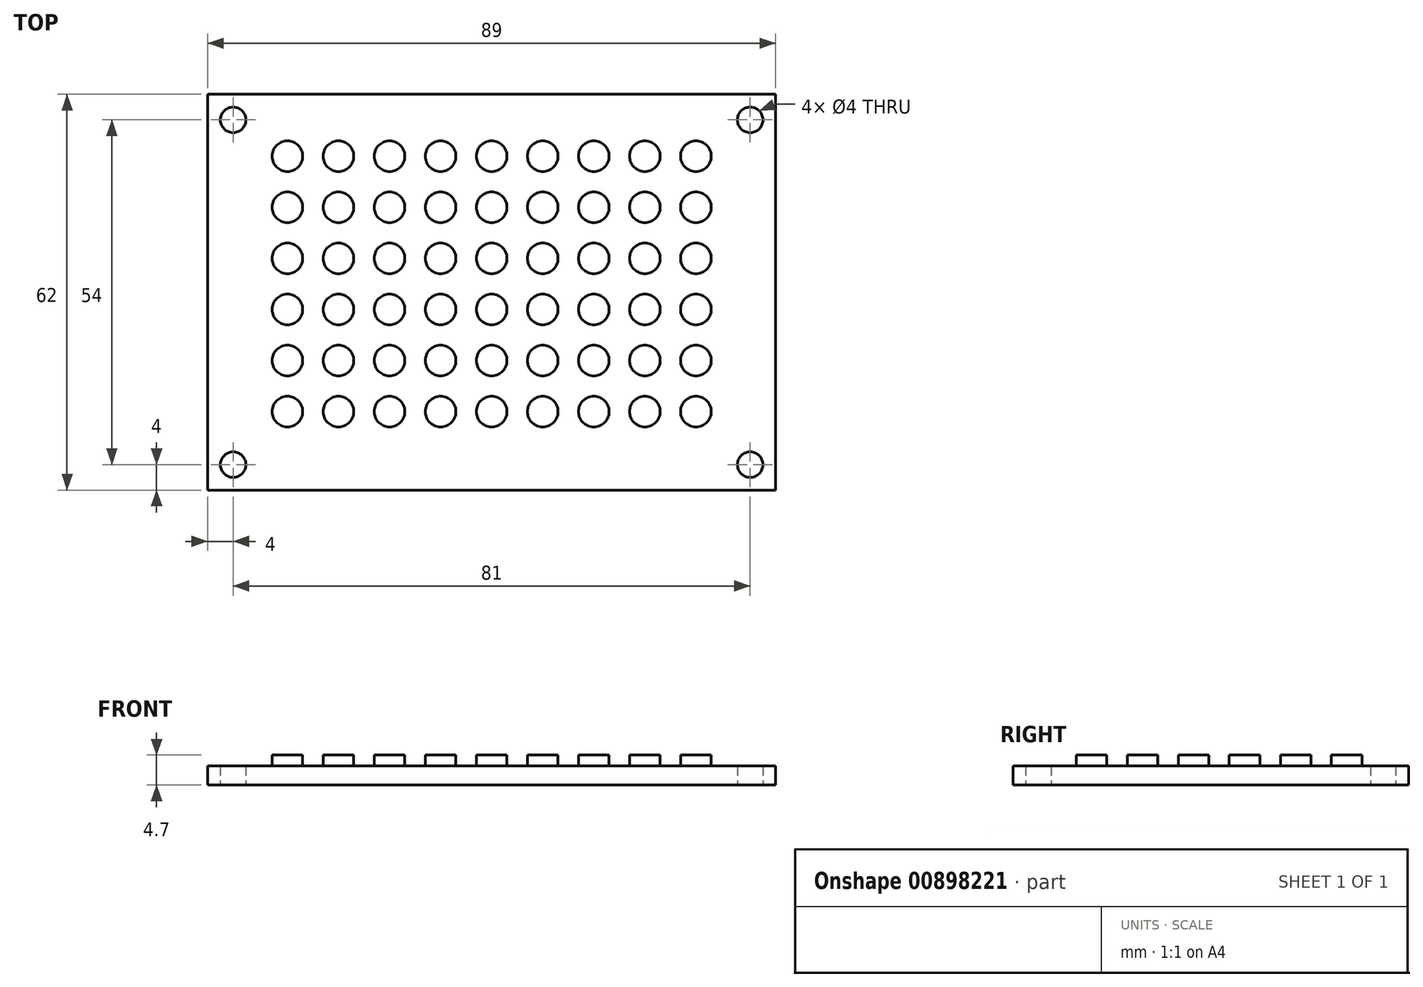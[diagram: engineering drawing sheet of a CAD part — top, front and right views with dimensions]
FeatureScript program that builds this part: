
annotation { "Feature Type Name" : "Feature", "Feature Type Description" : "" }
export const myFeature = defineFeature(function(context is Context, id is Id, definition is map)
    precondition{}
    {
        {
            var Q0;
            Q0=qCreatedBy(makeId("Top.planeOp"),FACE);
            var sketch = newSketch(context, id + "F0", { "sketchPlane" : qUnion([Q0])});
            skLineSegment(sketch, "E0.bottom", {"start": v(44.5, -31) * mm, "end": v(-44.5, -31) * mm});
            skLineSegment(sketch, "E0.top", {"start": v(44.5, 31) * mm, "end": v(-44.5, 31) * mm});
            skLineSegment(sketch, "E0.left", {"start": v(44.5, -31) * mm, "end": v(44.5, 31) * mm});
            skLineSegment(sketch, "E0.right", {"start": v(-44.5, -31) * mm, "end": v(-44.5, 31) * mm});
            skPoint(sketch, "E0.middle", {"position": v(0, 0) * mm});
            skCircle(sketch, "E1", {"center": v(40.5, 27) * mm, "radius": 2 * mm});
            skCircle(sketch, "E2.MirrorC", {"center": v(-40.5, 27) * mm, "radius": 2 * mm});
            skPoint(sketch, "E3.endSnap0", {"position": v(44.5, 0) * mm});
            skCircle(sketch, "E4.MirrorC", {"center": v(40.5, -27) * mm, "radius": 2 * mm});
            skCircle(sketch, "E5.MirrorC", {"center": v(-40.5, -27) * mm, "radius": 2 * mm});
            skSolve(sketch);
        }
        {
            var Q0;
            Q0=makeQuery(id+"F0.imprint","IMPRINT",FACE,{"disambiguationData":[TD([[makeQuery(id+"F0.imprint","IMPRINT",EDGE,{"derivedFrom":sQuery(id+"F0.wireOp",EDGE,"E0.bottom")}),-1.0]])]});
            extrude(context, id + "F1", {"entities" : qUnion([Q0]), "depth" : 3 * mm, "offsetDistance" : 25 * mm});
        }
        {
            var Q0;
            Q0=makeQuery(id+"F1.opExtrude","CAP_FACE",FACE,{"disambiguationData":[OSD([sQuery(id+"F0.wireOp",EDGE,"E0.bottom"),sQuery(id+"F0.wireOp",EDGE,"E0.top"),sQuery(id+"F0.wireOp",EDGE,"E0.left"),sQuery(id+"F0.wireOp",EDGE,"E0.right"),sQuery(id+"F0.wireOp",EDGE,"E2.MirrorC"),sQuery(id+"F0.wireOp",EDGE,"E4.MirrorC"),sQuery(id+"F0.wireOp",EDGE,"E1"),sQuery(id+"F0.wireOp",EDGE,"E5.MirrorC")])],"isStart":false});
            var sketch = newSketch(context, id + "F2", { "sketchPlane" : qUnion([Q0])});
            skCircle(sketch, "E6", {"center": v(0, 21.3) * mm, "radius": 2.4 * mm});
            skCircle(sketch, "E7.1.0.0", {"center": v(8, 21.3) * mm, "radius": 2.4 * mm});
            skCircle(sketch, "E7.2.0.0", {"center": v(16, 21.3) * mm, "radius": 2.4 * mm});
            skCircle(sketch, "E7.3.0.0", {"center": v(24, 21.3) * mm, "radius": 2.4 * mm});
            skCircle(sketch, "E7.4.0.0", {"center": v(32, 21.3) * mm, "radius": 2.4 * mm});
            skCircle(sketch, "E8.1.0.0", {"center": v(-8, 21.3) * mm, "radius": 2.4 * mm});
            skCircle(sketch, "E8.2.0.0", {"center": v(-16, 21.3) * mm, "radius": 2.4 * mm});
            skCircle(sketch, "E8.3.0.0", {"center": v(-24, 21.3) * mm, "radius": 2.4 * mm});
            skCircle(sketch, "E8.4.0.0", {"center": v(-32, 21.3) * mm, "radius": 2.4 * mm});
            skCircle(sketch, "E9.1.0.0", {"center": v(-8, 13.3) * mm, "radius": 2.4 * mm});
            skCircle(sketch, "E9.1.0.1", {"center": v(32, 13.3) * mm, "radius": 2.4 * mm});
            skCircle(sketch, "E9.1.0.2", {"center": v(8, 13.3) * mm, "radius": 2.4 * mm});
            skCircle(sketch, "E9.1.0.3", {"center": v(-32, 13.3) * mm, "radius": 2.4 * mm});
            skCircle(sketch, "E9.1.0.4", {"center": v(24, 13.3) * mm, "radius": 2.4 * mm});
            skCircle(sketch, "E9.1.0.5", {"center": v(16, 13.3) * mm, "radius": 2.4 * mm});
            skCircle(sketch, "E9.1.0.6", {"center": v(-24, 13.3) * mm, "radius": 2.4 * mm});
            skCircle(sketch, "E9.1.0.7", {"center": v(-16, 13.3) * mm, "radius": 2.4 * mm});
            skCircle(sketch, "E9.1.0.8", {"center": v(0, 13.3) * mm, "radius": 2.4 * mm});
            skCircle(sketch, "E9.2.0.0", {"center": v(-8, 5.3) * mm, "radius": 2.4 * mm});
            skCircle(sketch, "E9.2.0.1", {"center": v(32, 5.3) * mm, "radius": 2.4 * mm});
            skCircle(sketch, "E9.2.0.2", {"center": v(8, 5.3) * mm, "radius": 2.4 * mm});
            skCircle(sketch, "E9.2.0.3", {"center": v(-32, 5.3) * mm, "radius": 2.4 * mm});
            skCircle(sketch, "E9.2.0.4", {"center": v(24, 5.3) * mm, "radius": 2.4 * mm});
            skCircle(sketch, "E9.2.0.5", {"center": v(16, 5.3) * mm, "radius": 2.4 * mm});
            skCircle(sketch, "E9.2.0.6", {"center": v(-24, 5.3) * mm, "radius": 2.4 * mm});
            skCircle(sketch, "E9.2.0.7", {"center": v(-16, 5.3) * mm, "radius": 2.4 * mm});
            skCircle(sketch, "E9.2.0.8", {"center": v(0, 5.3) * mm, "radius": 2.4 * mm});
            skCircle(sketch, "E9.3.0.0", {"center": v(-8, -2.7) * mm, "radius": 2.4 * mm});
            skCircle(sketch, "E9.3.0.1", {"center": v(32, -2.7) * mm, "radius": 2.4 * mm});
            skCircle(sketch, "E9.3.0.2", {"center": v(8, -2.7) * mm, "radius": 2.4 * mm});
            skCircle(sketch, "E9.3.0.3", {"center": v(-32, -2.7) * mm, "radius": 2.4 * mm});
            skCircle(sketch, "E9.3.0.4", {"center": v(24, -2.7) * mm, "radius": 2.4 * mm});
            skCircle(sketch, "E9.3.0.5", {"center": v(16, -2.7) * mm, "radius": 2.4 * mm});
            skCircle(sketch, "E9.3.0.6", {"center": v(-24, -2.7) * mm, "radius": 2.4 * mm});
            skCircle(sketch, "E9.3.0.7", {"center": v(-16, -2.7) * mm, "radius": 2.4 * mm});
            skCircle(sketch, "E9.3.0.8", {"center": v(0, -2.7) * mm, "radius": 2.4 * mm});
            skCircle(sketch, "E9.4.0.0", {"center": v(-8, -10.7) * mm, "radius": 2.4 * mm});
            skCircle(sketch, "E9.4.0.1", {"center": v(32, -10.7) * mm, "radius": 2.4 * mm});
            skCircle(sketch, "E9.4.0.2", {"center": v(8, -10.7) * mm, "radius": 2.4 * mm});
            skCircle(sketch, "E9.4.0.3", {"center": v(-32, -10.7) * mm, "radius": 2.4 * mm});
            skCircle(sketch, "E9.4.0.4", {"center": v(24, -10.7) * mm, "radius": 2.4 * mm});
            skCircle(sketch, "E9.4.0.5", {"center": v(16, -10.7) * mm, "radius": 2.4 * mm});
            skCircle(sketch, "E9.4.0.6", {"center": v(-24, -10.7) * mm, "radius": 2.4 * mm});
            skCircle(sketch, "E9.4.0.7", {"center": v(-16, -10.7) * mm, "radius": 2.4 * mm});
            skCircle(sketch, "E9.4.0.8", {"center": v(0, -10.7) * mm, "radius": 2.4 * mm});
            skCircle(sketch, "E9.5.0.0", {"center": v(-8, -18.7) * mm, "radius": 2.4 * mm});
            skCircle(sketch, "E9.5.0.1", {"center": v(32, -18.7) * mm, "radius": 2.4 * mm});
            skCircle(sketch, "E9.5.0.2", {"center": v(8, -18.7) * mm, "radius": 2.4 * mm});
            skCircle(sketch, "E9.5.0.3", {"center": v(-32, -18.7) * mm, "radius": 2.4 * mm});
            skCircle(sketch, "E9.5.0.4", {"center": v(24, -18.7) * mm, "radius": 2.4 * mm});
            skCircle(sketch, "E9.5.0.5", {"center": v(16, -18.7) * mm, "radius": 2.4 * mm});
            skCircle(sketch, "E9.5.0.6", {"center": v(-24, -18.7) * mm, "radius": 2.4 * mm});
            skCircle(sketch, "E9.5.0.7", {"center": v(-16, -18.7) * mm, "radius": 2.4 * mm});
            skCircle(sketch, "E9.5.0.8", {"center": v(0, -18.7) * mm, "radius": 2.4 * mm});
            skLineSegment(sketch, "E9.direction1", {"start": v(-32, 21.3) * mm, "end": v(-32, 13.3) * mm, "construction": true});
            skSolve(sketch);
        }
        {
            var Q0;
            Q0=makeQuery(id+"F2.imprint","IMPRINT",FACE,{"disambiguationData":[TD([[makeQuery(id+"F2.imprint","IMPRINT",EDGE,{"derivedFrom":sQuery(id+"F2.wireOp",EDGE,"E7.2.0.0")}),1.0]])]});
            var Q1;
            Q1=makeQuery(id+"F2.imprint","IMPRINT",FACE,{"disambiguationData":[TD([[makeQuery(id+"F2.imprint","IMPRINT",EDGE,{"derivedFrom":sQuery(id+"F2.wireOp",EDGE,"E7.3.0.0")}),1.0]])]});
            var Q2;
            Q2=makeQuery(id+"F2.imprint","IMPRINT",FACE,{"disambiguationData":[TD([[makeQuery(id+"F2.imprint","IMPRINT",EDGE,{"derivedFrom":sQuery(id+"F2.wireOp",EDGE,"E9.4.0.8")}),1.0]])]});
            var Q3;
            Q3=makeQuery(id+"F2.imprint","IMPRINT",FACE,{"disambiguationData":[TD([[makeQuery(id+"F2.imprint","IMPRINT",EDGE,{"derivedFrom":sQuery(id+"F2.wireOp",EDGE,"E9.5.0.2")}),1.0]])]});
            var Q4;
            Q4=makeQuery(id+"F2.imprint","IMPRINT",FACE,{"disambiguationData":[TD([[makeQuery(id+"F2.imprint","IMPRINT",EDGE,{"derivedFrom":sQuery(id+"F2.wireOp",EDGE,"E9.5.0.4")}),1.0]])]});
            var Q5;
            Q5=makeQuery(id+"F2.imprint","IMPRINT",FACE,{"disambiguationData":[TD([[makeQuery(id+"F2.imprint","IMPRINT",EDGE,{"derivedFrom":sQuery(id+"F2.wireOp",EDGE,"E9.3.0.8")}),1.0]])]});
            var Q6;
            Q6=makeQuery(id+"F2.imprint","IMPRINT",FACE,{"disambiguationData":[TD([[makeQuery(id+"F2.imprint","IMPRINT",EDGE,{"derivedFrom":sQuery(id+"F2.wireOp",EDGE,"E9.4.0.0")}),1.0]])]});
            var Q7;
            Q7=makeQuery(id+"F2.imprint","IMPRINT",FACE,{"disambiguationData":[TD([[makeQuery(id+"F2.imprint","IMPRINT",EDGE,{"derivedFrom":sQuery(id+"F2.wireOp",EDGE,"E9.1.0.6")}),1.0]])]});
            var Q8;
            Q8=makeQuery(id+"F2.imprint","IMPRINT",FACE,{"disambiguationData":[TD([[makeQuery(id+"F2.imprint","IMPRINT",EDGE,{"derivedFrom":sQuery(id+"F2.wireOp",EDGE,"E9.5.0.1")}),1.0]])]});
            var Q9;
            Q9=makeQuery(id+"F2.imprint","IMPRINT",FACE,{"disambiguationData":[TD([[makeQuery(id+"F2.imprint","IMPRINT",EDGE,{"derivedFrom":sQuery(id+"F2.wireOp",EDGE,"E9.5.0.6")}),1.0]])]});
            var Q10;
            Q10=makeQuery(id+"F2.imprint","IMPRINT",FACE,{"disambiguationData":[TD([[makeQuery(id+"F2.imprint","IMPRINT",EDGE,{"derivedFrom":sQuery(id+"F2.wireOp",EDGE,"E9.1.0.2")}),1.0]])]});
            var Q11;
            Q11=makeQuery(id+"F2.imprint","IMPRINT",FACE,{"disambiguationData":[TD([[makeQuery(id+"F2.imprint","IMPRINT",EDGE,{"derivedFrom":sQuery(id+"F2.wireOp",EDGE,"E7.4.0.0")}),1.0]])]});
            var Q12;
            Q12=makeQuery(id+"F2.imprint","IMPRINT",FACE,{"disambiguationData":[TD([[makeQuery(id+"F2.imprint","IMPRINT",EDGE,{"derivedFrom":sQuery(id+"F2.wireOp",EDGE,"E9.4.0.5")}),1.0]])]});
            var Q13;
            Q13=makeQuery(id+"F2.imprint","IMPRINT",FACE,{"disambiguationData":[TD([[makeQuery(id+"F2.imprint","IMPRINT",EDGE,{"derivedFrom":sQuery(id+"F2.wireOp",EDGE,"E9.5.0.5")}),1.0]])]});
            var Q14;
            Q14=makeQuery(id+"F2.imprint","IMPRINT",FACE,{"disambiguationData":[TD([[makeQuery(id+"F2.imprint","IMPRINT",EDGE,{"derivedFrom":sQuery(id+"F2.wireOp",EDGE,"E9.4.0.4")}),1.0]])]});
            var Q15;
            Q15=makeQuery(id+"F2.imprint","IMPRINT",FACE,{"disambiguationData":[TD([[makeQuery(id+"F2.imprint","IMPRINT",EDGE,{"derivedFrom":sQuery(id+"F2.wireOp",EDGE,"E9.5.0.0")}),1.0]])]});
            var Q16;
            Q16=makeQuery(id+"F2.imprint","IMPRINT",FACE,{"disambiguationData":[TD([[makeQuery(id+"F2.imprint","IMPRINT",EDGE,{"derivedFrom":sQuery(id+"F2.wireOp",EDGE,"E9.1.0.1")}),1.0]])]});
            var Q17;
            Q17=makeQuery(id+"F2.imprint","IMPRINT",FACE,{"disambiguationData":[TD([[makeQuery(id+"F2.imprint","IMPRINT",EDGE,{"derivedFrom":sQuery(id+"F2.wireOp",EDGE,"E8.4.0.0")}),1.0]])]});
            var Q18;
            Q18=makeQuery(id+"F2.imprint","IMPRINT",FACE,{"disambiguationData":[TD([[makeQuery(id+"F2.imprint","IMPRINT",EDGE,{"derivedFrom":sQuery(id+"F2.wireOp",EDGE,"E9.5.0.7")}),1.0]])]});
            var Q19;
            Q19=makeQuery(id+"F2.imprint","IMPRINT",FACE,{"disambiguationData":[TD([[makeQuery(id+"F2.imprint","IMPRINT",EDGE,{"derivedFrom":sQuery(id+"F2.wireOp",EDGE,"E6")}),1.0]])]});
            var Q20;
            Q20=makeQuery(id+"F2.imprint","IMPRINT",FACE,{"disambiguationData":[TD([[makeQuery(id+"F2.imprint","IMPRINT",EDGE,{"derivedFrom":sQuery(id+"F2.wireOp",EDGE,"E8.2.0.0")}),1.0]])]});
            var Q21;
            Q21=makeQuery(id+"F2.imprint","IMPRINT",FACE,{"disambiguationData":[TD([[makeQuery(id+"F2.imprint","IMPRINT",EDGE,{"derivedFrom":sQuery(id+"F2.wireOp",EDGE,"E9.4.0.7")}),1.0]])]});
            var Q22;
            Q22=makeQuery(id+"F2.imprint","IMPRINT",FACE,{"disambiguationData":[TD([[makeQuery(id+"F2.imprint","IMPRINT",EDGE,{"derivedFrom":sQuery(id+"F2.wireOp",EDGE,"E8.1.0.0")}),1.0]])]});
            var Q23;
            Q23=makeQuery(id+"F2.imprint","IMPRINT",FACE,{"disambiguationData":[TD([[makeQuery(id+"F2.imprint","IMPRINT",EDGE,{"derivedFrom":sQuery(id+"F2.wireOp",EDGE,"E9.4.0.3")}),1.0]])]});
            var Q24;
            Q24=makeQuery(id+"F2.imprint","IMPRINT",FACE,{"disambiguationData":[TD([[makeQuery(id+"F2.imprint","IMPRINT",EDGE,{"derivedFrom":sQuery(id+"F2.wireOp",EDGE,"E7.1.0.0")}),1.0]])]});
            var Q25;
            Q25=makeQuery(id+"F2.imprint","IMPRINT",FACE,{"disambiguationData":[TD([[makeQuery(id+"F2.imprint","IMPRINT",EDGE,{"derivedFrom":sQuery(id+"F2.wireOp",EDGE,"E9.5.0.3")}),1.0]])]});
            var Q26;
            Q26=makeQuery(id+"F2.imprint","IMPRINT",FACE,{"disambiguationData":[TD([[makeQuery(id+"F2.imprint","IMPRINT",EDGE,{"derivedFrom":sQuery(id+"F2.wireOp",EDGE,"E9.1.0.0")}),1.0]])]});
            var Q27;
            Q27=makeQuery(id+"F2.imprint","IMPRINT",FACE,{"disambiguationData":[TD([[makeQuery(id+"F2.imprint","IMPRINT",EDGE,{"derivedFrom":sQuery(id+"F2.wireOp",EDGE,"E8.3.0.0")}),1.0]])]});
            var Q28;
            Q28=makeQuery(id+"F2.imprint","IMPRINT",FACE,{"disambiguationData":[TD([[makeQuery(id+"F2.imprint","IMPRINT",EDGE,{"derivedFrom":sQuery(id+"F2.wireOp",EDGE,"E9.4.0.6")}),1.0]])]});
            var Q29;
            Q29=makeQuery(id+"F2.imprint","IMPRINT",FACE,{"disambiguationData":[TD([[makeQuery(id+"F2.imprint","IMPRINT",EDGE,{"derivedFrom":sQuery(id+"F2.wireOp",EDGE,"E9.4.0.1")}),1.0]])]});
            var Q30;
            Q30=makeQuery(id+"F2.imprint","IMPRINT",FACE,{"disambiguationData":[TD([[makeQuery(id+"F2.imprint","IMPRINT",EDGE,{"derivedFrom":sQuery(id+"F2.wireOp",EDGE,"E9.5.0.8")}),1.0]])]});
            var Q31;
            Q31=makeQuery(id+"F2.imprint","IMPRINT",FACE,{"disambiguationData":[TD([[makeQuery(id+"F2.imprint","IMPRINT",EDGE,{"derivedFrom":sQuery(id+"F2.wireOp",EDGE,"E9.4.0.2")}),1.0]])]});
            var Q32;
            Q32=makeQuery(id+"F2.imprint","IMPRINT",FACE,{"disambiguationData":[TD([[makeQuery(id+"F2.imprint","IMPRINT",EDGE,{"derivedFrom":sQuery(id+"F2.wireOp",EDGE,"E9.3.0.7")}),1.0]])]});
            var Q33;
            Q33=makeQuery(id+"F2.imprint","IMPRINT",FACE,{"disambiguationData":[TD([[makeQuery(id+"F2.imprint","IMPRINT",EDGE,{"derivedFrom":sQuery(id+"F2.wireOp",EDGE,"E9.3.0.6")}),1.0]])]});
            var Q34;
            Q34=makeQuery(id+"F2.imprint","IMPRINT",FACE,{"disambiguationData":[TD([[makeQuery(id+"F2.imprint","IMPRINT",EDGE,{"derivedFrom":sQuery(id+"F2.wireOp",EDGE,"E9.3.0.5")}),1.0]])]});
            var Q35;
            Q35=makeQuery(id+"F2.imprint","IMPRINT",FACE,{"disambiguationData":[TD([[makeQuery(id+"F2.imprint","IMPRINT",EDGE,{"derivedFrom":sQuery(id+"F2.wireOp",EDGE,"E9.3.0.4")}),1.0]])]});
            var Q36;
            Q36=makeQuery(id+"F2.imprint","IMPRINT",FACE,{"disambiguationData":[TD([[makeQuery(id+"F2.imprint","IMPRINT",EDGE,{"derivedFrom":sQuery(id+"F2.wireOp",EDGE,"E9.3.0.3")}),1.0]])]});
            var Q37;
            Q37=makeQuery(id+"F2.imprint","IMPRINT",FACE,{"disambiguationData":[TD([[makeQuery(id+"F2.imprint","IMPRINT",EDGE,{"derivedFrom":sQuery(id+"F2.wireOp",EDGE,"E9.3.0.2")}),1.0]])]});
            var Q38;
            Q38=makeQuery(id+"F2.imprint","IMPRINT",FACE,{"disambiguationData":[TD([[makeQuery(id+"F2.imprint","IMPRINT",EDGE,{"derivedFrom":sQuery(id+"F2.wireOp",EDGE,"E9.3.0.1")}),1.0]])]});
            var Q39;
            Q39=makeQuery(id+"F2.imprint","IMPRINT",FACE,{"disambiguationData":[TD([[makeQuery(id+"F2.imprint","IMPRINT",EDGE,{"derivedFrom":sQuery(id+"F2.wireOp",EDGE,"E9.3.0.0")}),1.0]])]});
            var Q40;
            Q40=makeQuery(id+"F2.imprint","IMPRINT",FACE,{"disambiguationData":[TD([[makeQuery(id+"F2.imprint","IMPRINT",EDGE,{"derivedFrom":sQuery(id+"F2.wireOp",EDGE,"E9.2.0.8")}),1.0]])]});
            var Q41;
            Q41=makeQuery(id+"F2.imprint","IMPRINT",FACE,{"disambiguationData":[TD([[makeQuery(id+"F2.imprint","IMPRINT",EDGE,{"derivedFrom":sQuery(id+"F2.wireOp",EDGE,"E9.2.0.7")}),1.0]])]});
            var Q42;
            Q42=makeQuery(id+"F2.imprint","IMPRINT",FACE,{"disambiguationData":[TD([[makeQuery(id+"F2.imprint","IMPRINT",EDGE,{"derivedFrom":sQuery(id+"F2.wireOp",EDGE,"E9.2.0.6")}),1.0]])]});
            var Q43;
            Q43=makeQuery(id+"F2.imprint","IMPRINT",FACE,{"disambiguationData":[TD([[makeQuery(id+"F2.imprint","IMPRINT",EDGE,{"derivedFrom":sQuery(id+"F2.wireOp",EDGE,"E9.2.0.5")}),1.0]])]});
            var Q44;
            Q44=makeQuery(id+"F2.imprint","IMPRINT",FACE,{"disambiguationData":[TD([[makeQuery(id+"F2.imprint","IMPRINT",EDGE,{"derivedFrom":sQuery(id+"F2.wireOp",EDGE,"E9.2.0.4")}),1.0]])]});
            var Q45;
            Q45=makeQuery(id+"F2.imprint","IMPRINT",FACE,{"disambiguationData":[TD([[makeQuery(id+"F2.imprint","IMPRINT",EDGE,{"derivedFrom":sQuery(id+"F2.wireOp",EDGE,"E9.2.0.3")}),1.0]])]});
            var Q46;
            Q46=makeQuery(id+"F2.imprint","IMPRINT",FACE,{"disambiguationData":[TD([[makeQuery(id+"F2.imprint","IMPRINT",EDGE,{"derivedFrom":sQuery(id+"F2.wireOp",EDGE,"E9.2.0.2")}),1.0]])]});
            var Q47;
            Q47=makeQuery(id+"F2.imprint","IMPRINT",FACE,{"disambiguationData":[TD([[makeQuery(id+"F2.imprint","IMPRINT",EDGE,{"derivedFrom":sQuery(id+"F2.wireOp",EDGE,"E9.2.0.1")}),1.0]])]});
            var Q48;
            Q48=makeQuery(id+"F2.imprint","IMPRINT",FACE,{"disambiguationData":[TD([[makeQuery(id+"F2.imprint","IMPRINT",EDGE,{"derivedFrom":sQuery(id+"F2.wireOp",EDGE,"E9.1.0.5")}),1.0]])]});
            var Q49;
            Q49=makeQuery(id+"F2.imprint","IMPRINT",FACE,{"disambiguationData":[TD([[makeQuery(id+"F2.imprint","IMPRINT",EDGE,{"derivedFrom":sQuery(id+"F2.wireOp",EDGE,"E9.2.0.0")}),1.0]])]});
            var Q50;
            Q50=makeQuery(id+"F2.imprint","IMPRINT",FACE,{"disambiguationData":[TD([[makeQuery(id+"F2.imprint","IMPRINT",EDGE,{"derivedFrom":sQuery(id+"F2.wireOp",EDGE,"E9.1.0.8")}),1.0]])]});
            var Q51;
            Q51=makeQuery(id+"F2.imprint","IMPRINT",FACE,{"disambiguationData":[TD([[makeQuery(id+"F2.imprint","IMPRINT",EDGE,{"derivedFrom":sQuery(id+"F2.wireOp",EDGE,"E9.1.0.7")}),1.0]])]});
            var Q52;
            Q52=makeQuery(id+"F2.imprint","IMPRINT",FACE,{"disambiguationData":[TD([[makeQuery(id+"F2.imprint","IMPRINT",EDGE,{"derivedFrom":sQuery(id+"F2.wireOp",EDGE,"E9.1.0.4")}),1.0]])]});
            var Q53;
            Q53=makeQuery(id+"F2.imprint","IMPRINT",FACE,{"disambiguationData":[TD([[makeQuery(id+"F2.imprint","IMPRINT",EDGE,{"derivedFrom":sQuery(id+"F2.wireOp",EDGE,"E9.1.0.3")}),1.0]])]});
            extrude(context, id + "F3", {"entities" : qUnion([Q0, Q1, Q2, Q3, Q4, Q5, Q6, Q7, Q8, Q9, Q10, Q11, Q12, Q13, Q14, Q15, Q16, Q17, Q18, Q19, Q20, Q21, Q22, Q23, Q24, Q25, Q26, Q27, Q28, Q29, Q30, Q31, Q32, Q33, Q34, Q35, Q36, Q37, Q38, Q39, Q40, Q41, Q42, Q43, Q44, Q45, Q46, Q47, Q48, Q49, Q50, Q51, Q52, Q53]), "operationType" : NewBodyOperationType.ADD, "depth" : 1.7 * mm, "offsetDistance" : 25 * mm});
        }
    });
